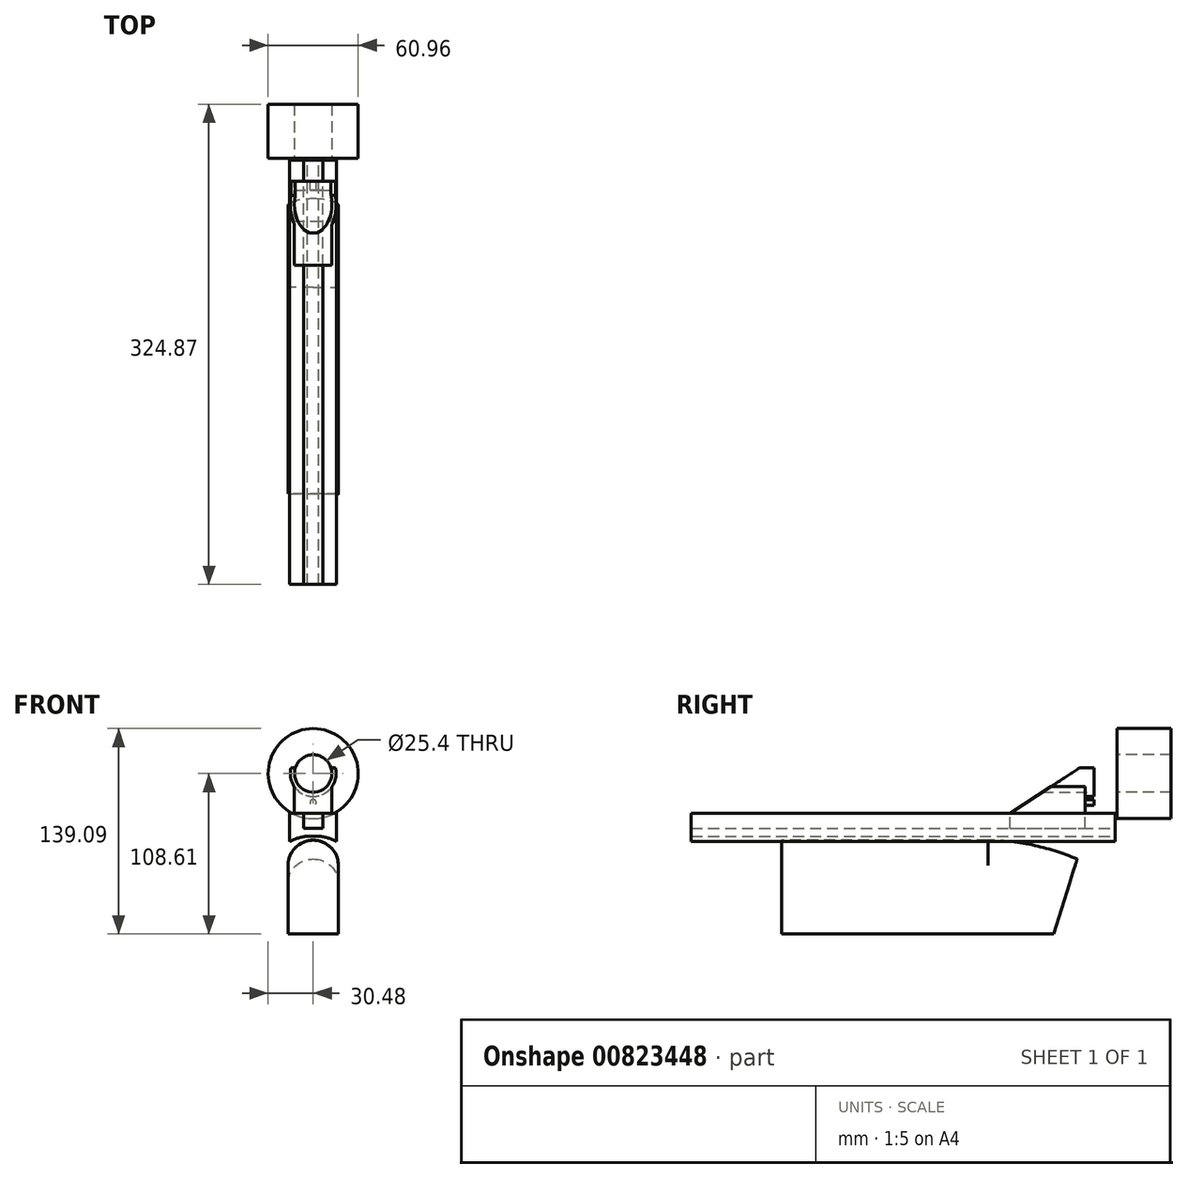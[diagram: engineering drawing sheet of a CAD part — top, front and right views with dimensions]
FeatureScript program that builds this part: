
annotation { "Feature Type Name" : "Feature", "Feature Type Description" : "" }
export const myFeature = defineFeature(function(context is Context, id is Id, definition is map)
    precondition{}
    {
        {
            var Q0;
            Q0=qCreatedBy(makeId("Front.planeOp"),FACE);
            var sketch = newSketch(context, id + "F0", { "sketchPlane" : qUnion([Q0])});
            skArc(sketch, "E0", {"start": v(-12.04, 4.04) * mm, "mid": v(0, -12.7) * mm, "end": v(12.04, 4.04) * mm});
            skArc(sketch, "E1", {"start": v(-14.96, 4.04) * mm, "mid": v(0, -15.5) * mm, "end": v(14.96, 4.04) * mm});
            skLineSegment(sketch, "E2.top", {"start": v(-12.7, -26.92) * mm, "end": v(12.7, -26.92) * mm});
            skLineSegment(sketch, "E2.left", {"start": v(-12.7, -8.88) * mm, "end": v(-12.7, -26.92) * mm});
            skLineSegment(sketch, "E2.right", {"start": v(12.7, -8.88) * mm, "end": v(12.7, -26.92) * mm});
            skLineSegment(sketch, "E3.bottom", {"start": v(6.43, -37.08) * mm, "end": v(-6.43, -37.08) * mm});
            skLineSegment(sketch, "E3.left", {"start": v(6.43, -37.08) * mm, "end": v(6.43, -26.92) * mm});
            skLineSegment(sketch, "E3.right", {"start": v(-6.43, -37.08) * mm, "end": v(-6.43, -26.92) * mm});
            skPoint(sketch, "E3.middle", {"position": v(0, -26.92) * mm});
            skLineSegment(sketch, "E4", {"start": v(-14.96, 4.04) * mm, "end": v(-12.04, 4.04) * mm});
            skLineSegment(sketch, "E5", {"start": v(14.96, 4.04) * mm, "end": v(12.04, 4.04) * mm});
            skLineSegment(sketch, "E6", {"start": v(-12.7, -26.92) * mm, "end": v(-15.87, -26.92) * mm});
            skLineSegment(sketch, "E7", {"start": v(-15.87, -26.92) * mm, "end": v(-15.87, -45.97) * mm});
            skLineSegment(sketch, "E8", {"start": v(15.88, -45.97) * mm, "end": v(15.88, -26.92) * mm});
            skLineSegment(sketch, "E9", {"start": v(15.87, -26.92) * mm, "end": v(12.7, -26.92) * mm});
            skArc(sketch, "E10", {"start": v(15.87, -45.97) * mm, "mid": v(10, -43.62) * mm, "end": v(3.8, -42.37) * mm});
            skLineSegment(sketch, "E11", {"start": v(-3.8, -42.37) * mm, "end": v(3.8, -42.37) * mm});
            skPoint(sketch, "E12", {"position": v(0, -42.37) * mm});
            skArc(sketch, "E13.trimOffspring", {"start": v(-3.8, -42.37) * mm, "mid": v(-10, -43.62) * mm, "end": v(-15.87, -45.97) * mm});
            skCircle(sketch, "E14", {"center": v(0, -19.56) * mm, "radius": 2.03 * mm});
            skSolve(sketch);
        }
        {
            var Q0;
            Q0=makeQuery(id+"F0.imprint","IMPRINT",FACE,{"disambiguationData":[TD([[makeQuery(id+"F0.imprint","IMPRINT",EDGE,{"derivedFrom":sQuery(id+"F0.wireOp",EDGE,"E3.bottom")}),1.0]])]});
            extrude(context, id + "F1", {"entities" : qUnion([Q0]), "depth" : 266.7 * mm, "offsetDistance" : 25.4 * mm, "hasSecondDirection" : true, "secondDirectionOppositeDirection" : true, "secondDirectionDepth" : 20.32 * mm});
        }
        {
            var Q0;
            {var subQ4=sQuery(id+"F0.wireOp",EDGE,"E2.left");Q0=makeQuery(id+"F0.imprint","IMPRINT",FACE,{"disambiguationData":[TD([[makeQuery(id+"F0.imprint","IMPRINT",EDGE,{"derivedFrom":subQ4}),1.0]])]});}
            var Q1;
            Q1=makeQuery(id+"F0.imprint","IMPRINT",FACE,{"disambiguationData":[TD([[makeQuery(id+"F0.imprint","IMPRINT",EDGE,{"derivedFrom":sQuery(id+"F0.wireOp",EDGE,"E3.bottom")}),-1.0]])]});
            extrude(context, id + "F2", {"entities" : qUnion([Q0, Q1]), "depth" : 50.8 * mm, "offsetDistance" : 25.4 * mm});
        }
        {
            var Q0;
            Q0=makeQuery(id+"F0.imprint","IMPRINT",FACE,{"disambiguationData":[TD([[makeQuery(id+"F0.imprint","IMPRINT",EDGE,{"derivedFrom":sQuery(id+"F0.wireOp",EDGE,"E0")}),-1.0]])]});
            var Q1;
            Q1=makeQuery(id+"F0.imprint","IMPRINT",FACE,{"disambiguationData":[TD([[makeQuery(id+"F0.imprint","IMPRINT",EDGE,{"derivedFrom":sQuery(id+"F0.wireOp",EDGE,"E14")}),1.0]])]});
            extrude(context, id + "F3", {"entities" : qUnion([Q0, Q1]), "operationType" : NewBodyOperationType.ADD, "depth" : 50.8 * mm, "offsetDistance" : 25.4 * mm, "hasSecondDirection" : true, "secondDirectionOppositeDirection" : true, "secondDirectionDepth" : 6.1 * mm});
        }
        {
            var Q0;
            Q0=qCreatedBy(makeId("Right.planeOp"),FACE);
            var sketch = newSketch(context, id + "F4", { "sketchPlane" : qUnion([Q0])});
            skLineSegment(sketch, "E15", {"start": v(-2.56, 4.61) * mm, "end": v(-50.8, -26.83) * mm});
            skLineSegment(sketch, "E16", {"start": v(-50.8, -26.83) * mm, "end": v(-53.63, -26.83) * mm});
            skLineSegment(sketch, "E17", {"start": v(-53.63, -26.83) * mm, "end": v(-53.63, 4.61) * mm});
            skLineSegment(sketch, "E18", {"start": v(-53.63, 4.61) * mm, "end": v(-2.56, 4.61) * mm});
            skSolve(sketch);
        }
        {
            var Q0;
            Q0=makeQuery(id+"F4.imprint","IMPRINT",FACE,{"disambiguationData":[TD([[makeQuery(id+"F4.imprint","IMPRINT",EDGE,{"derivedFrom":sQuery(id+"F4.wireOp",EDGE,"E15")}),-1.0]])]});
            extrude(context, id + "F5", {"entities" : qUnion([Q0]), "operationType" : NewBodyOperationType.REMOVE, "endBound" : BoundingType.SYMMETRIC, "depth" : 50.8 * mm, "offsetDistance" : 25.4 * mm});
        }
        {
            var Q0;
            Q0=qCreatedBy(makeId("Front.planeOp"),FACE);
            var sketch = newSketch(context, id + "F6", { "sketchPlane" : qUnion([Q0])});
            skCircle(sketch, "E19", {"center": v(0, 0) * mm, "radius": 30.48 * mm});
            skCircle(sketch, "E20", {"center": v(0, 0) * mm, "radius": 12.7 * mm});
            skSolve(sketch);
        }
        {
            var Q0;
            Q0=makeQuery(id+"F6.imprint","IMPRINT",FACE,{"disambiguationData":[TD([[makeQuery(id+"F6.imprint","IMPRINT",EDGE,{"derivedFrom":sQuery(id+"F6.wireOp",EDGE,"E19")}),1.0]])]});
            extrude(context, id + "F7", {"entities" : qUnion([Q0]), "oppositeDirection" : true, "depth" : 58.17 * mm, "offsetDistance" : 25.4 * mm, "hasSecondDirection" : true, "secondDirectionOppositeDirection" : true, "secondDirectionDepth" : 21.59 * mm});
        }
        {
            var Q0;
            Q0=qCreatedBy(makeId("Right.planeOp"),FACE);
            var sketch = newSketch(context, id + "F8", { "sketchPlane" : qUnion([Q0])});
            skLineSegment(sketch, "E21", {"start": v(-205.47, -45.11) * mm, "end": v(-65.77, -45.11) * mm});
            skLineSegment(sketch, "E22", {"start": v(-205.47, -45.11) * mm, "end": v(-205.47, -108.61) * mm});
            skLineSegment(sketch, "E23", {"start": v(-205.47, -108.61) * mm, "end": v(-21.32, -108.61) * mm});
            skLineSegment(sketch, "E24", {"start": v(-21.32, -108.61) * mm, "end": v(-5.45, -57.81) * mm});
            skFitSpline(sketch, "E25", {"points": [v(-65.77, -45.11) * mm, v(-5.45, -57.81) * mm], "startDerivative": vector(59.04, 1.2) * mm, "endDerivative": vector(50.53, -21.88) * mm});
            skSolve(sketch);
        }
        {
            var Q0;
            Q0=makeQuery(id+"F8.imprint","IMPRINT",FACE,{"disambiguationData":[TD([[makeQuery(id+"F8.imprint","IMPRINT",EDGE,{"derivedFrom":sQuery(id+"F8.wireOp",EDGE,"E21")}),-1.0]])]});
            extrude(context, id + "F9", {"entities" : qUnion([Q0]), "endBound" : BoundingType.SYMMETRIC, "depth" : 34.04 * mm, "offsetDistance" : 25.4 * mm});
        }
        {
            var Q0;
            Q0=makeQuery(id+"F9.opExtrude","CAP_EDGE",EDGE,{"disambiguationData":[OSD([sQuery(id+"F8.wireOp",EDGE,"E25")])],"isStart":false});
            var Q1;
            Q1=makeQuery(id+"F9.opExtrude","CAP_EDGE",EDGE,{"disambiguationData":[OSD([sQuery(id+"F8.wireOp",EDGE,"E25")])],"isStart":true});
            fillet(context, id + "F10", {"entities" : qUnion([Q0, Q1]), "radius" : 17.02 * mm, "tangentPropagation" : true, "allowEdgeOverflow" : false});
        }
    });
